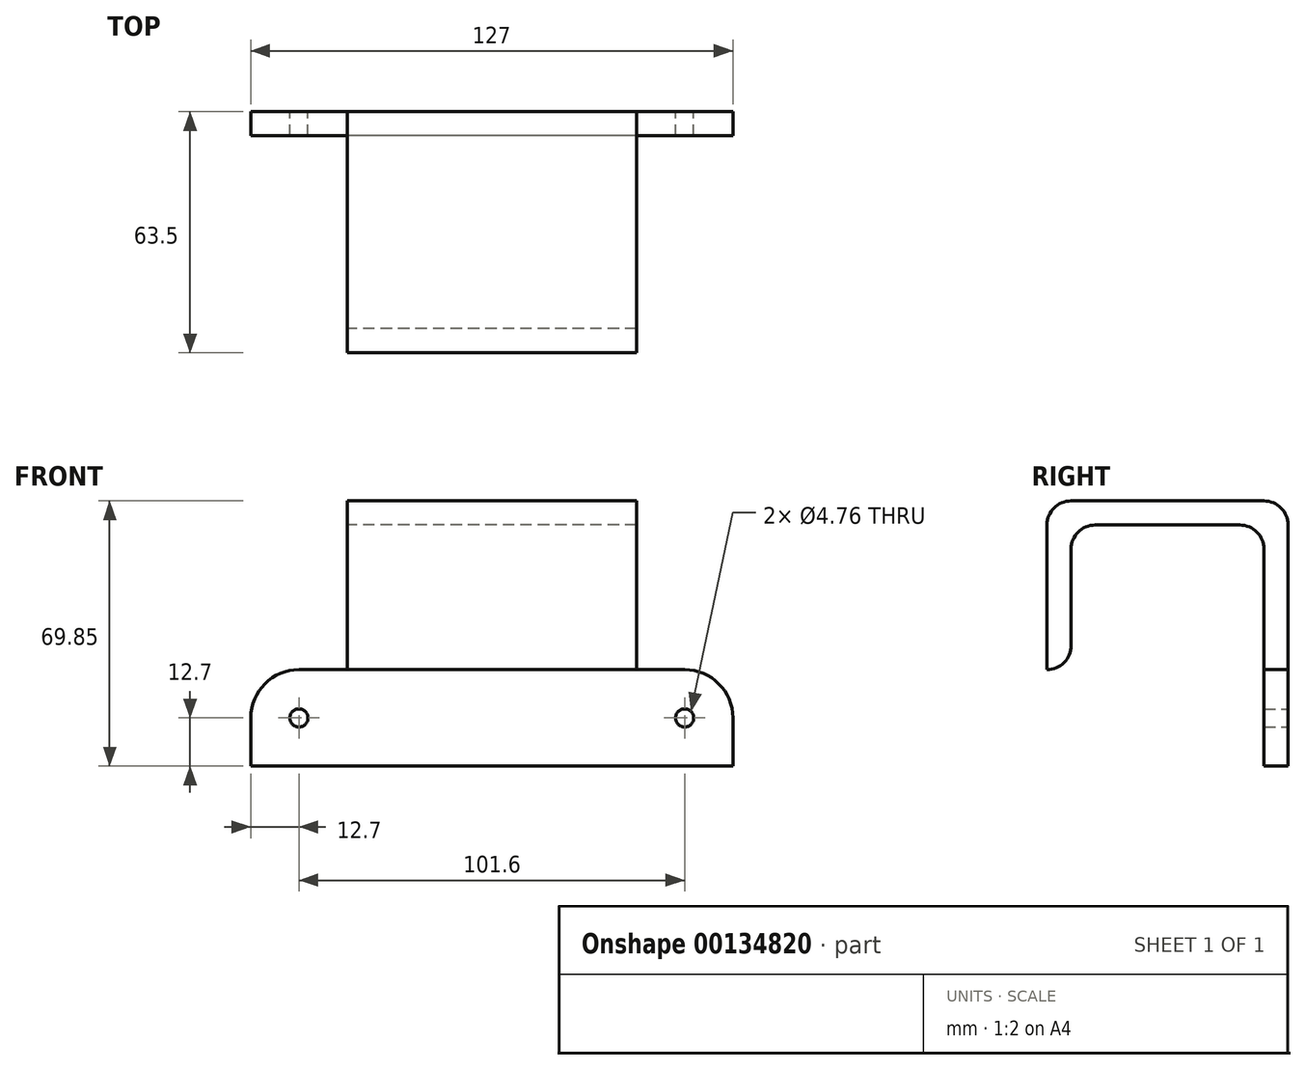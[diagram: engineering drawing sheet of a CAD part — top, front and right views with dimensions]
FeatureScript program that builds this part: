
annotation { "Feature Type Name" : "Feature", "Feature Type Description" : "" }
export const myFeature = defineFeature(function(context is Context, id is Id, definition is map)
    precondition{}
    {
        {
            var Q0;
            Q0=qCreatedBy(makeId("Front.planeOp"),FACE);
            var sketch = newSketch(context, id + "F0", { "sketchPlane" : qUnion([Q0])});
            skLineSegment(sketch, "E0.bottom", {"start": v(63.5, 12.7) * mm, "end": v(-63.5, 12.7) * mm});
            skLineSegment(sketch, "E0.top", {"start": v(63.5, -12.7) * mm, "end": v(-63.5, -12.7) * mm});
            skLineSegment(sketch, "E0.left", {"start": v(63.5, 12.7) * mm, "end": v(63.5, -12.7) * mm});
            skLineSegment(sketch, "E0.right", {"start": v(-63.5, 12.7) * mm, "end": v(-63.5, -12.7) * mm});
            skPoint(sketch, "E0.middle", {"position": v(0, 0) * mm});
            skLineSegment(sketch, "E1", {"start": v(-63.5, 0) * mm, "end": v(63.5, 0) * mm});
            skCircle(sketch, "E2", {"center": v(-50.8, 0) * mm, "radius": 2.38 * mm});
            skCircle(sketch, "E3", {"center": v(50.8, 0) * mm, "radius": 2.38 * mm});
            skLineSegment(sketch, "E4", {"start": v(-50.8, 0) * mm, "end": v(50.8, 0) * mm});
            skSolve(sketch);
        }
        {
            var Q0;
            {var subQ5=sQuery(id+"F0.wireOp",EDGE,"E0.bottom");Q0=makeQuery(id+"F0.imprint","IMPRINT",FACE,{"disambiguationData":[TD([[makeQuery(id+"F0.imprint","IMPRINT",EDGE,{"derivedFrom":subQ5}),1.0]])]});}
            var Q1;
            {var subQ9=sQuery(id+"F0.wireOp",EDGE,"E0.top");Q1=makeQuery(id+"F0.imprint","IMPRINT",FACE,{"disambiguationData":[TD([[makeQuery(id+"F0.imprint","IMPRINT",EDGE,{"derivedFrom":subQ9}),-1.0]])]});}
            extrude(context, id + "F1", {"entities" : qUnion([Q0, Q1]), "depth" : 6.35 * mm});
        }
        {
            var Q0;
            Q0=makeQuery(id+"F1.opExtrude","SWEPT_EDGE",EDGE,{"disambiguationData":[OSD([sQuery(id+"F0.wireOp",EDGE,"E0.bottom"),sQuery(id+"F0.wireOp",EDGE,"E0.right")])]});
            var Q1;
            Q1=makeQuery(id+"F1.opExtrude","SWEPT_EDGE",EDGE,{"disambiguationData":[OSD([sQuery(id+"F0.wireOp",EDGE,"E0.bottom"),sQuery(id+"F0.wireOp",EDGE,"E0.left")])]});
            fillet(context, id + "F2", {"entities" : qUnion([Q0, Q1]), "radius" : 12.7 * mm, "tangentPropagation" : true, "allowEdgeOverflow" : false});
        }
        {
            var Q0;
            Q0=qCreatedBy(makeId("Right.planeOp"),FACE);
            var sketch = newSketch(context, id + "F3", { "sketchPlane" : qUnion([Q0])});
            skLineSegment(sketch, "E5", {"start": v(0, 57.15) * mm, "end": v(0, 12.7) * mm});
            skLineSegment(sketch, "E6", {"start": v(0, 57.15) * mm, "end": v(-63.5, 57.15) * mm});
            skLineSegment(sketch, "E7", {"start": v(-63.5, 57.15) * mm, "end": v(-63.5, 12.7) * mm});
            skLineSegment(sketch, "E8", {"start": v(-63.5, 12.7) * mm, "end": v(-57.15, 12.7) * mm});
            skLineSegment(sketch, "E9", {"start": v(-57.15, 12.7) * mm, "end": v(-57.15, 50.8) * mm});
            skLineSegment(sketch, "E10", {"start": v(-57.15, 50.8) * mm, "end": v(-6.35, 50.8) * mm});
            skLineSegment(sketch, "E11", {"start": v(-6.35, 50.8) * mm, "end": v(-6.35, 12.7) * mm});
            skLineSegment(sketch, "E12", {"start": v(0, 12.7) * mm, "end": v(-6.35, 12.7) * mm});
            skSolve(sketch);
        }
        {
            var Q0;
            Q0 = qSketchRegion(id + "F3", true);
            extrude(context, id + "F4", {"entities" : qUnion([Q0]), "operationType" : NewBodyOperationType.ADD, "endBound" : BoundingType.SYMMETRIC, "depth" : 76.2 * mm, "hasSecondDirection" : true, "secondDirectionOppositeDirection" : true, "secondDirectionDepth" : 25.4 * mm});
        }
        {
            var Q0;
            Q0=makeQuery(id+"F4.opExtrude","SWEPT_EDGE",EDGE,{"disambiguationData":[OSD([sQuery(id+"F3.wireOp",EDGE,"E5"),sQuery(id+"F3.wireOp",EDGE,"E6")])]});
            var Q1;
            Q1=makeQuery(id+"F4.opExtrude","SWEPT_EDGE",EDGE,{"disambiguationData":[OSD([sQuery(id+"F3.wireOp",EDGE,"E6"),sQuery(id+"F3.wireOp",EDGE,"E7")])]});
            var Q2;
            Q2=makeQuery(id+"F4.opExtrude","SWEPT_EDGE",EDGE,{"disambiguationData":[OSD([sQuery(id+"F3.wireOp",EDGE,"E10"),sQuery(id+"F3.wireOp",EDGE,"E11")])]});
            var Q3;
            Q3=makeQuery(id+"F4.opExtrude","SWEPT_EDGE",EDGE,{"disambiguationData":[OSD([sQuery(id+"F3.wireOp",EDGE,"E9"),sQuery(id+"F3.wireOp",EDGE,"E10")])]});
            var Q4;
            Q4=makeQuery(id+"F4.opExtrude","SWEPT_EDGE",EDGE,{"disambiguationData":[OSD([sQuery(id+"F3.wireOp",EDGE,"E8"),sQuery(id+"F3.wireOp",EDGE,"E9")])]});
            fillet(context, id + "F5", {"entities" : qUnion([Q0, Q1, Q2, Q3, Q4]), "radius" : 6.35 * mm, "tangentPropagation" : true, "allowEdgeOverflow" : false});
        }
    });
